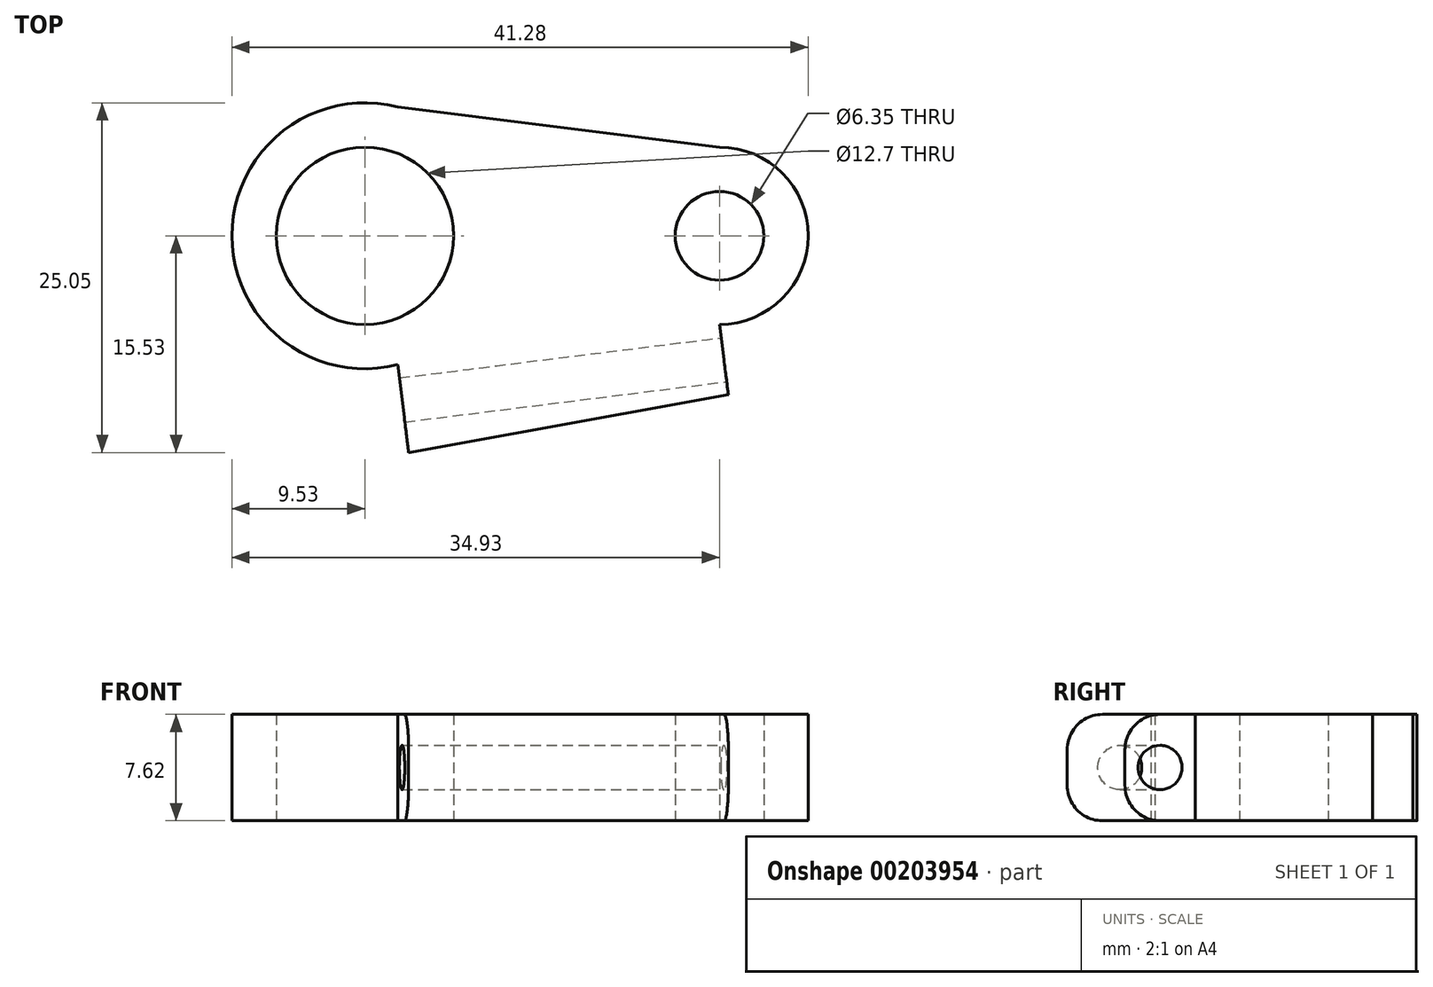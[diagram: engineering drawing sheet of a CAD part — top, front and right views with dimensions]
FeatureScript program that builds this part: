
annotation { "Feature Type Name" : "Feature", "Feature Type Description" : "" }
export const myFeature = defineFeature(function(context is Context, id is Id, definition is map)
    precondition{}
    {
        {
            var Q0;
            Q0=qCreatedBy(makeId("Top.planeOp"),FACE);
            var sketch = newSketch(context, id + "F0", { "sketchPlane" : qUnion([Q0])});
            skLineSegment(sketch, "E0", {"start": v(0, 0) * mm, "end": v(25.4, 0) * mm});
            skCircle(sketch, "E1", {"center": v(0, 0) * mm, "radius": 6.35 * mm});
            skArc(sketch, "E2", {"start": v(2.34, 9.23) * mm, "mid": v(-9.53, 0) * mm, "end": v(2.34, -9.23) * mm});
            skCircle(sketch, "E3", {"center": v(25.4, 0) * mm, "radius": 3.18 * mm});
            skArc(sketch, "E4", {"start": v(25.4, -6.35) * mm, "mid": v(31.75, 0) * mm, "end": v(25.4, 6.35) * mm});
            skLineSegment(sketch, "E5", {"start": v(0, 9.53) * mm, "end": v(25.4, 6.35) * mm});
            skLineSegment(sketch, "E6", {"start": v(0, -9.53) * mm, "end": v(25.4, -6.35) * mm});
            skSolve(sketch);
        }
        {
            var Q0;
            Q0 = qSketchRegion(id + "F0", true);
            extrude(context, id + "F1", {"entities" : qUnion([Q0]), "depth" : 7.62 * mm});
        }
        {
            var Q0;
            Q0=makeQuery(id+"F1.opExtrude","CAP_FACE",FACE,{"disambiguationData":[OSD([sQuery(id+"F0.wireOp",EDGE,"E1"),sQuery(id+"F0.wireOp",EDGE,"E2"),sQuery(id+"F0.wireOp",EDGE,"E3"),sQuery(id+"F0.wireOp",EDGE,"E4"),sQuery(id+"F0.wireOp",EDGE,"E5"),sQuery(id+"F0.wireOp",EDGE,"E6")])],"isStart":false});
            var sketch = newSketch(context, id + "F2", { "sketchPlane" : qUnion([Q0])});
            skLineSegment(sketch, "E7", {"start": v(25.4, -6.35) * mm, "end": v(26.03, -11.4) * mm});
            skLineSegment(sketch, "E8", {"start": v(2.34, -9.23) * mm, "end": v(3.13, -15.53) * mm});
            skLineSegment(sketch, "E9", {"start": v(3.13, -15.53) * mm, "end": v(26.03, -11.4) * mm});
            skSolve(sketch);
        }
        {
            var Q0;
            Q0 = qSketchRegion(id + "F2", true);
            var Q1;
            Q1=makeQuery(id+"F2.imprint","IMPRINT",FACE,{"disambiguationData":[TD([[makeQuery(id+"F2.imprint","IMPRINT",EDGE,{"derivedFrom":sQuery(id+"F2.wireOp",EDGE,"E7")}),-1.0]])]});
            extrude(context, id + "F3", {"entities" : qUnion([Q0, Q1]), "operationType" : NewBodyOperationType.ADD, "oppositeDirection" : true, "depth" : 7.62 * mm});
        }
        {
            var Q0;
            Q0=makeQuery(id+"F3.opExtrude","SWEPT_FACE",FACE,{"disambiguationData":[OSD([sQuery(id+"F2.wireOp",EDGE,"E7")])]});
            var sketch = newSketch(context, id + "F4", { "sketchPlane" : qUnion([Q0])});
            skCircle(sketch, "E10", {"center": v(-12, 3.81) * mm, "radius": 1.59 * mm});
            skPoint(sketch, "E10.centerSnap0", {"position": v(-9.45, 3.81) * mm});
            skSolve(sketch);
        }
        {
            var Q0;
            Q0 = qSketchRegion(id + "F4", true);
            extrude(context, id + "F5", {"entities" : qUnion([Q0]), "operationType" : NewBodyOperationType.REMOVE, "oppositeDirection" : true, "depth" : 25.4 * mm});
        }
        {
            var Q0;
            Q0=makeQuery(id+"F3.opExtrude","CAP_EDGE",EDGE,{"disambiguationData":[OSD([sQuery(id+"F2.wireOp",EDGE,"E9")])],"isStart":true});
            var Q1;
            Q1=makeQuery(id+"F3.opExtrude","CAP_EDGE",EDGE,{"disambiguationData":[OSD([sQuery(id+"F2.wireOp",EDGE,"E9")])],"isStart":false});
            fillet(context, id + "F6", {"entities" : qUnion([Q0, Q1]), "radius" : 2.54 * mm, "tangentPropagation" : true, "allowEdgeOverflow" : false});
        }
    });
